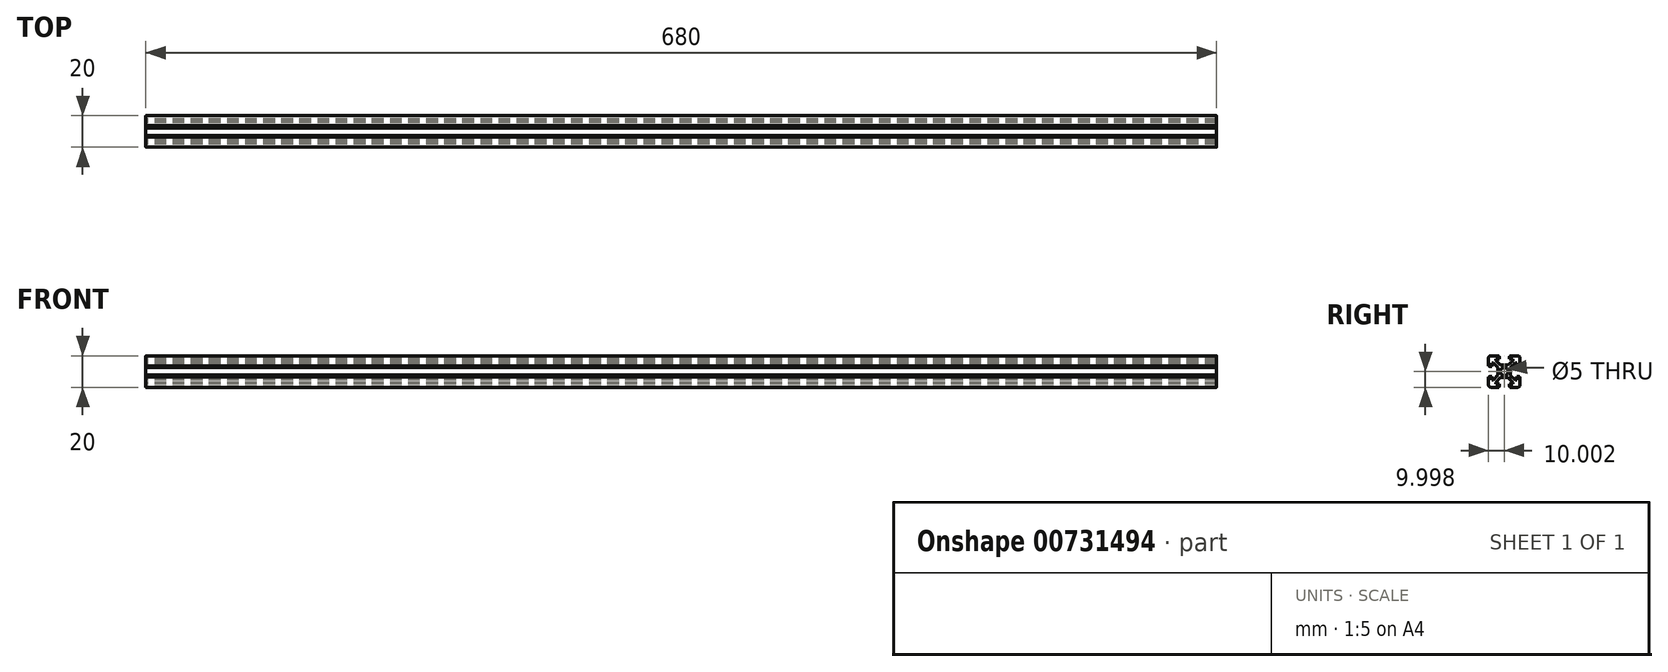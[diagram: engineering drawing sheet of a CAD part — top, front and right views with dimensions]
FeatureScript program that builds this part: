
annotation { "Feature Type Name" : "Feature", "Feature Type Description" : "" }
export const myFeature = defineFeature(function(context is Context, id is Id, definition is map)
    precondition{}
    {
        {
            var Q0;
            Q0=qCreatedBy(makeId("Right.planeOp"),FACE);
            var sketch = newSketch(context, id + "F0", { "sketchPlane" : qUnion([Q0])});
            skLineSegment(sketch, "E0.bottom", {"start": v(-8.49, 9.99) * mm, "end": v(-3.59, 9.99) * mm});
            skLineSegment(sketch, "E0.top", {"start": v(-8.49, -10.01) * mm, "end": v(-3.59, -10.01) * mm});
            skLineSegment(sketch, "E0.left", {"start": v(-9.99, 8.49) * mm, "end": v(-9.99, 3.59) * mm});
            skLineSegment(sketch, "E0.right", {"start": v(10.01, 8.49) * mm, "end": v(10.01, 3.59) * mm});
            skArc(sketch, "E1.filletArc", {"start": v(-8.49, 9.99) * mm, "mid": v(-9.55, 9.55) * mm, "end": v(-9.99, 8.49) * mm});
            skArc(sketch, "E2.filletArc", {"start": v(10.01, 8.49) * mm, "mid": v(9.57, 9.55) * mm, "end": v(8.51, 9.99) * mm});
            skArc(sketch, "E3.filletArc", {"start": v(8.51, -10.01) * mm, "mid": v(9.57, -9.57) * mm, "end": v(10.01, -8.51) * mm});
            skArc(sketch, "E4.filletArc", {"start": v(-9.99, -8.51) * mm, "mid": v(-9.55, -9.57) * mm, "end": v(-8.49, -10.01) * mm});
            skLineSegment(sketch, "E5.bottom", {"start": v(-5.49, 7.99) * mm, "end": v(-3.09, 7.99) * mm});
            skLineSegment(sketch, "E5.top", {"start": v(-5.49, -8.01) * mm, "end": v(-3.09, -8.01) * mm});
            skLineSegment(sketch, "E5.left", {"start": v(-7.99, 5.49) * mm, "end": v(-7.99, 3.09) * mm});
            skLineSegment(sketch, "E5.right", {"start": v(8.01, 5.49) * mm, "end": v(8.01, 3.09) * mm});
            skCircle(sketch, "E6", {"center": v(0.01, -0.01) * mm, "radius": 2.5 * mm});
            skLineSegment(sketch, "E7.right", {"start": v(5.51, -8.01) * mm, "end": v(5.51, -6.93) * mm});
            skLineSegment(sketch, "E8.top", {"start": v(8.01, 5.49) * mm, "end": v(7.02, 5.49) * mm});
            skLineSegment(sketch, "E9.bottom", {"start": v(-2.57, 3.99) * mm, "end": v(2.3, 3.99) * mm});
            skLineSegment(sketch, "E9.top", {"start": v(-2.65, -3.81) * mm, "end": v(2.4, -3.81) * mm});
            skLineSegment(sketch, "E9.left", {"start": v(-3.99, 2.57) * mm, "end": v(-3.99, -2.3) * mm});
            skLineSegment(sketch, "E9.right", {"start": v(3.81, 2.65) * mm, "end": v(3.81, -2.4) * mm});
            skLineSegment(sketch, "E10.trimOffspring", {"start": v(8.01, -5.51) * mm, "end": v(6.93, -5.51) * mm});
            skLineSegment(sketch, "E11.trimOffspring", {"start": v(-5.49, -8.01) * mm, "end": v(-5.49, -7.02) * mm});
            skLineSegment(sketch, "E12.left", {"start": v(-3.09, 9.49) * mm, "end": v(-3.09, 7.99) * mm});
            skLineSegment(sketch, "E12.right", {"start": v(3.11, 9.49) * mm, "end": v(3.11, 7.99) * mm});
            skLineSegment(sketch, "E13.trimOffspring", {"start": v(3.61, 9.99) * mm, "end": v(8.51, 9.99) * mm});
            skLineSegment(sketch, "E14.trimOffspring", {"start": v(3.11, 7.99) * mm, "end": v(5.51, 7.99) * mm});
            skLineSegment(sketch, "E15.left", {"start": v(-3.09, -9.51) * mm, "end": v(-3.09, -8.01) * mm});
            skLineSegment(sketch, "E15.right", {"start": v(3.11, -9.51) * mm, "end": v(3.11, -8.01) * mm});
            skLineSegment(sketch, "E16.trimOffspring", {"start": v(3.11, -8.01) * mm, "end": v(5.51, -8.01) * mm});
            skLineSegment(sketch, "E17.trimOffspring", {"start": v(3.61, -10.01) * mm, "end": v(8.51, -10.01) * mm});
            skLineSegment(sketch, "E18.bottom", {"start": v(9.51, 3.09) * mm, "end": v(8.01, 3.09) * mm});
            skLineSegment(sketch, "E18.top", {"start": v(9.51, -3.11) * mm, "end": v(8.01, -3.11) * mm});
            skLineSegment(sketch, "E19.trimOffspring", {"start": v(8.01, -3.11) * mm, "end": v(8.01, -5.51) * mm});
            skLineSegment(sketch, "E20.trimOffspring", {"start": v(10.01, -3.61) * mm, "end": v(10.01, -8.51) * mm});
            skLineSegment(sketch, "E21.bottom", {"start": v(-9.49, 3.09) * mm, "end": v(-7.99, 3.09) * mm});
            skLineSegment(sketch, "E21.top", {"start": v(-9.49, -3.11) * mm, "end": v(-7.99, -3.11) * mm});
            skLineSegment(sketch, "E22.trimOffspring", {"start": v(-9.99, -3.61) * mm, "end": v(-9.99, -8.51) * mm});
            skLineSegment(sketch, "E23.trimOffspring", {"start": v(-7.99, -3.11) * mm, "end": v(-7.99, -5.51) * mm});
            skLineSegment(sketch, "E24.top", {"start": v(-3.59, -9.51) * mm, "end": v(-3.09, -9.51) * mm});
            skLineSegment(sketch, "E24.left", {"start": v(-3.59, -10.01) * mm, "end": v(-3.59, -9.51) * mm});
            skLineSegment(sketch, "E24.right", {"start": v(3.61, -10.01) * mm, "end": v(3.61, -9.51) * mm});
            skLineSegment(sketch, "E25.trimOffspring", {"start": v(3.11, -9.51) * mm, "end": v(3.61, -9.51) * mm});
            skLineSegment(sketch, "E26.trimOffspring", {"start": v(-6.9, 5.49) * mm, "end": v(-7.99, 5.49) * mm});
            skLineSegment(sketch, "E27.trimOffspring", {"start": v(-5.49, 6.9) * mm, "end": v(-5.49, 7.99) * mm});
            skLineSegment(sketch, "E28.trimOffspring", {"start": v(-6.82, -5.51) * mm, "end": v(-7.99, -5.51) * mm});
            skLineSegment(sketch, "E29.trimOffspring", {"start": v(5.51, 6.82) * mm, "end": v(5.51, 7.99) * mm});
            skLineSegment(sketch, "E30.bottom", {"start": v(-9.99, 3.59) * mm, "end": v(-9.49, 3.59) * mm});
            skLineSegment(sketch, "E30.top", {"start": v(-9.99, -3.61) * mm, "end": v(-9.49, -3.61) * mm});
            skLineSegment(sketch, "E30.right", {"start": v(-9.49, 3.59) * mm, "end": v(-9.49, 3.09) * mm});
            skLineSegment(sketch, "E31.trimOffspring", {"start": v(-9.49, -3.11) * mm, "end": v(-9.49, -3.61) * mm});
            skLineSegment(sketch, "E32.top", {"start": v(-3.59, 9.49) * mm, "end": v(-3.09, 9.49) * mm});
            skLineSegment(sketch, "E32.left", {"start": v(-3.59, 9.99) * mm, "end": v(-3.59, 9.49) * mm});
            skLineSegment(sketch, "E32.right", {"start": v(3.61, 9.99) * mm, "end": v(3.61, 9.49) * mm});
            skLineSegment(sketch, "E33.trimOffspring", {"start": v(3.11, 9.49) * mm, "end": v(3.61, 9.49) * mm});
            skLineSegment(sketch, "E34", {"start": v(9.51, 3.09) * mm, "end": v(9.51, 3.59) * mm});
            skLineSegment(sketch, "E35", {"start": v(9.51, 3.59) * mm, "end": v(10.01, 3.59) * mm});
            skLineSegment(sketch, "E36", {"start": v(9.51, -3.11) * mm, "end": v(9.51, -3.61) * mm});
            skLineSegment(sketch, "E37", {"start": v(9.51, -3.61) * mm, "end": v(10.01, -3.61) * mm});
            skLineSegment(sketch, "E38.0", {"start": v(5.51, 6.82) * mm, "end": v(2.3, 3.99) * mm});
            skLineSegment(sketch, "E39.0", {"start": v(7.02, 5.49) * mm, "end": v(3.81, 2.65) * mm});
            skLineSegment(sketch, "E40.0", {"start": v(-6.9, 5.49) * mm, "end": v(-3.99, 2.57) * mm});
            skLineSegment(sketch, "E41.0", {"start": v(-5.49, 6.9) * mm, "end": v(-2.57, 3.99) * mm});
            skLineSegment(sketch, "E42.0", {"start": v(-5.49, -7.02) * mm, "end": v(-2.65, -3.81) * mm});
            skLineSegment(sketch, "E43.0", {"start": v(-6.82, -5.51) * mm, "end": v(-3.99, -2.3) * mm});
            skLineSegment(sketch, "E44.0", {"start": v(6.93, -5.51) * mm, "end": v(3.81, -2.4) * mm});
            skLineSegment(sketch, "E45.0", {"start": v(5.51, -6.93) * mm, "end": v(2.4, -3.81) * mm});
            skSolve(sketch);
        }
        {
            var Q0;
            Q0=qSketchRegion(id+"F0",true);
            extrude(context, id + "F1", {"entities" : qUnion([Q0]), "depth" : 680 * mm, "offsetDistance" : 25 * mm});
        }
    });
